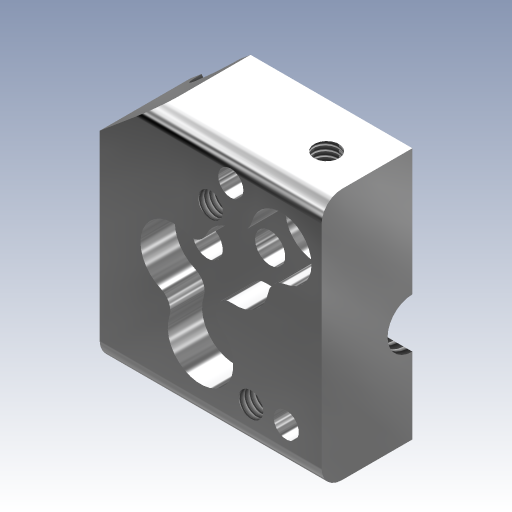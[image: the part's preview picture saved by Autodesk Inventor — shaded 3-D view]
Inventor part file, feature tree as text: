
AUTODESK INVENTOR PART (.ipt)
format: ipt  version: 2023.3 (Build 273359000, 359)  size: 440,320 bytes
history: native  units: mm (DEFAULTED — no unit token found)
features: other x10, sketch x8, hole x2, fillet x2, extrude x1
ambient origin geometry x1: Ursprung
bodies: Volumenkörper4 (feature_tree)
feature tree (23):
  other  "BT001_huenin20_23_Fiberprinter-Hotend_Heizblock_Seite1.ipt"
  sketch  "Skizze7"  dims[d1=3.0mm d2=10.0mm d3=6.5mm d4=3.4mm d5=90.0deg d6=8.0mm d7=20.594885mm d8=2.0mm d9=3.5mm d10=3.5mm]
  hole  "Bohrung1"  [1 undecoded]
  fillet  "Rundung1"  Radius=3.5mm
  hole  "Bohrung2"  [1 undecoded]
  extrude  "Extrusion1"  Depth=10.0mm TaperAngle=0.0deg
  fillet  "Rundung2"  Radius=1.55mm
  other  "YZ-Ebene"
  other  "XZ-Ebene"
  other  "XY-Ebene"
  other  "X-Achse"
  other  "Y-Achse"
  other  "Z-Achse"
  other  "Mittelpunkt"
  sketch  "Skizze3"  dims[d0=10.0mm]
  sketch  "Skizze19"  dims[d22=0.8mm d23=10.0mm d24=0.0mm d25=1.55mm]
  sketch  "Skizze20"  dims[d26=90.0deg]
  sketch  "Skizze21"  dims[d27=3.5mm]
  sketch  "Skizze22"  dims[d28=1.0mm d29=0.15mm d30=0.25mm d31=0.375mm d32=14.3117mm d33=0.75mm d34=20.594885mm d35=0.0625mm d36=0.75mm d37=0.375mm]
  other  "Volumenkörper4::BT001_huenin20_23_Fiberprinter-Hotend_Heizblock_Seite1.ipt"
  other  "Bezeichnung2"
  sketch  "Skizze8"  dims[d11=6.108652mm]
  sketch  "Skizze9"  dims[d12=2.459mm d13=10.0mm d14=4.0mm d15=2.0mm d16=90.0deg d17=5.0mm d18=0.0mm d19=0.8mm d20=0.8mm]
note: 2 required parameter values undecoded (feature->parameter linkage not recoverable at this tier; creation-order binding heuristic only, values carry confidence <= 0.55)
